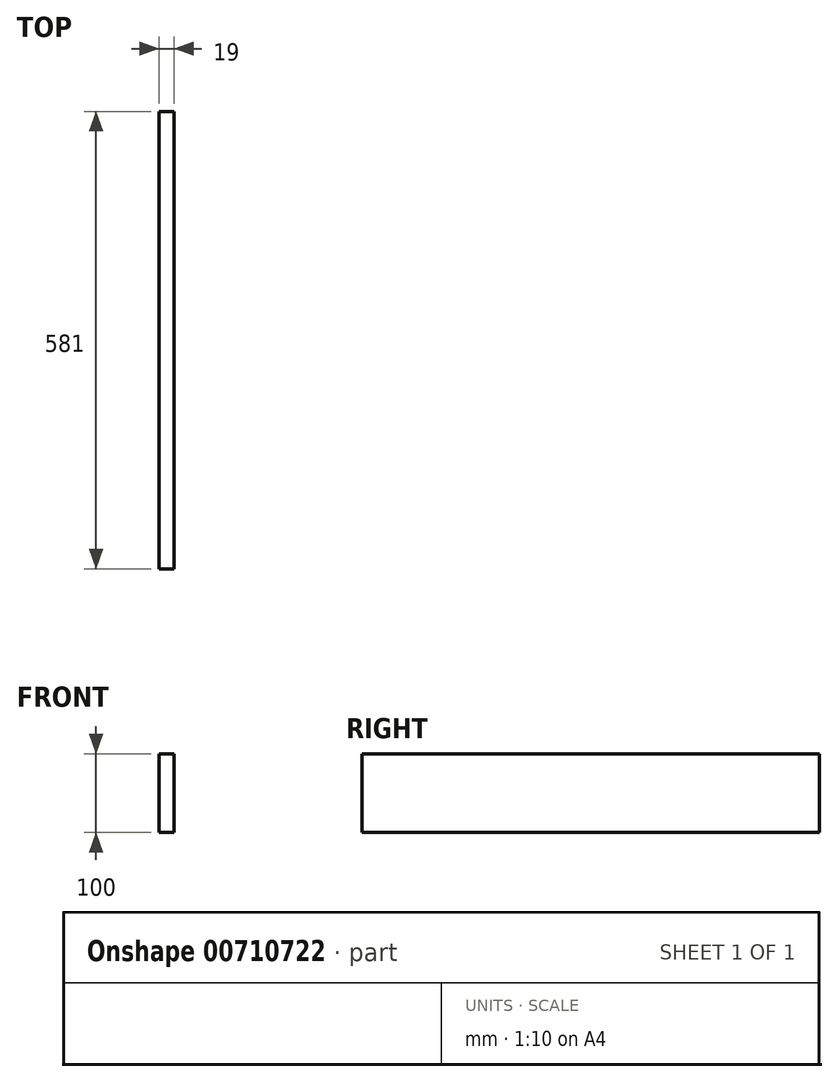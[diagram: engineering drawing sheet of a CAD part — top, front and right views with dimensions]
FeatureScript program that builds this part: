
annotation { "Feature Type Name" : "Feature", "Feature Type Description" : "" }
export const myFeature = defineFeature(function(context is Context, id is Id, definition is map)
    precondition{}
    {
        {
            var Q0;
            Q0=qCreatedBy(makeId("Front.planeOp"),FACE);
            var sketch = newSketch(context, id + "F0", { "sketchPlane" : qUnion([Q0])});
            skLineSegment(sketch, "E0.bottom", {"start": v(0, 0) * mm, "end": v(19, 0) * mm});
            skLineSegment(sketch, "E0.top", {"start": v(0, 100) * mm, "end": v(19, 100) * mm});
            skLineSegment(sketch, "E0.left", {"start": v(0, 0) * mm, "end": v(0, 100) * mm});
            skLineSegment(sketch, "E0.right", {"start": v(19, 0) * mm, "end": v(19, 100) * mm});
            skSolve(sketch);
        }
        {
            var Q0;
            Q0 = qSketchRegion(id + "F0", true);
            extrude(context, id + "F1", {"entities" : qUnion([Q0]), "depth" : (600 - 19) * mm, "offsetDistance" : 25 * mm});
        }
    });
